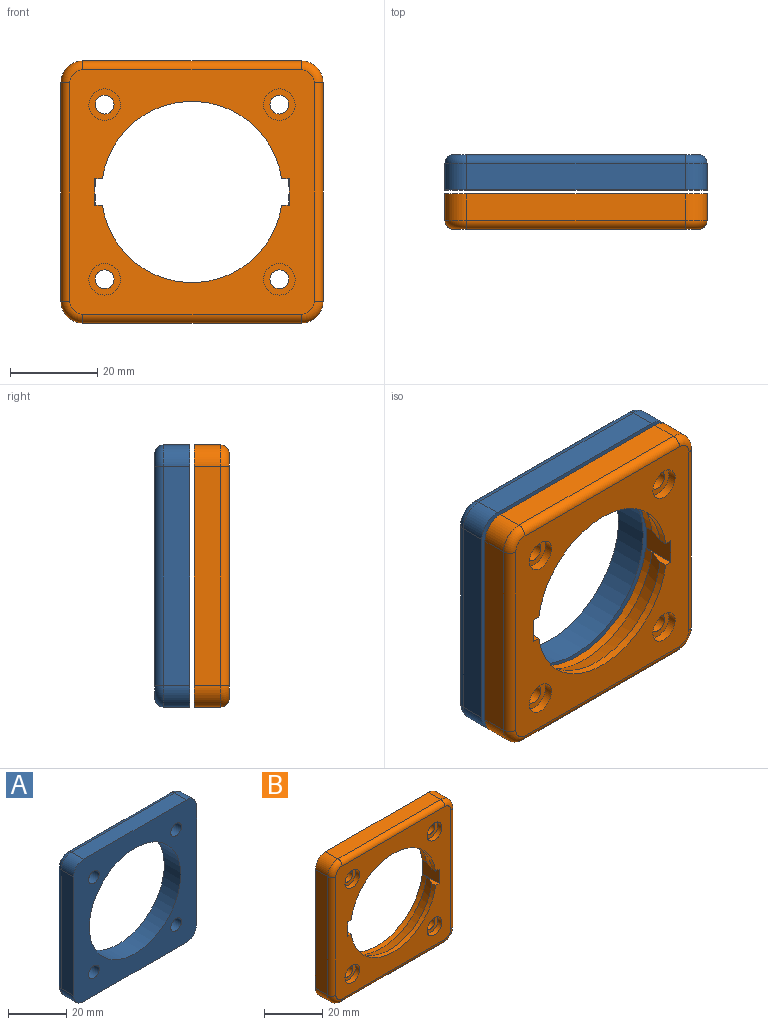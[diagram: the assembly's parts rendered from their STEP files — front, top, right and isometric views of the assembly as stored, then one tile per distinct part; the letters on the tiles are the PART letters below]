
ASSEMBLY  parts=2 mates=1
PART A: 23 faces, bbox 60.8x8x60.8 mm
  f0: plane 50x6mm, normal (-1,0,0), area 300mm2, adj f10,f11,f14,f22
  f1: plane 50x6mm, normal (0,0,1), area 300mm2, adj f10,f11,f12,f18
  f2: plane 50x6mm, normal (1,0,0), area 300mm2, adj f10,f12,f13,f15
  f3: cylinder r=22.25mm len=44.5mm, axis (0,-1,0), area 1118.4mm2, adj f9,f10
  f4: plane 50x6mm, normal (0,0,-1), area 300mm2, adj f10,f13,f14,f19
  f5: cylinder r=2.6mm len=8mm, axis (0,-1,0), area 130.7mm2, adj f9,f10
  f6: cylinder r=2.6mm len=8mm, axis (0,-1,0), area 130.7mm2, adj f9,f10
  f7: cylinder r=2.6mm len=8mm, axis (0,-1,0), area 130.7mm2, adj f9,f10
  f8: cylinder r=2.6mm len=8mm, axis (0,-1,0), area 130.7mm2, adj f9,f10
  f9: plane 56x56mm, normal (0,1,0), area 1488mm2, adj f3,f5,f6,f7,f8,f15,f16,f17
  f10: plane 60x60mm, normal (0,-1,0), area 1938.3mm2, adj f0,f1,f2,f3,f4,f5,f6,f7
  f11: cylinder r=5mm len=6mm, axis (0,1,0), area 47.1mm2, adj f0,f1,f10,f20
  f12: cylinder r=5mm len=6mm, axis (0,-1,0), area 47.1mm2, adj f1,f2,f10,f16
  f13: cylinder r=5mm len=6mm, axis (0,1,0), area 47.1mm2, adj f2,f4,f10,f17
  f14: cylinder r=5mm len=6mm, axis (0,-1,0), area 47.1mm2, adj f0,f4,f10,f21
  f15: cylinder r=2mm len=50mm, axis (0,0,1), area 157.1mm2, adj f2,f9,f16,f17
  f16: torus R=3mm, axis (0,1,0), area 21.1mm2, adj f9,f12,f15,f18
  f17: torus R=3mm, axis (0,1,0), area 21.1mm2, adj f9,f13,f15,f19
  f18: cylinder r=2mm len=50mm, axis (-1,0,0), area 157.1mm2, adj f1,f9,f16,f20
  f19: cylinder r=2mm len=50mm, axis (1,0,0), area 157.1mm2, adj f4,f9,f17,f21
  f20: torus R=3mm, axis (0,1,0), area 21.1mm2, adj f9,f11,f18,f22
  f21: torus R=3mm, axis (0,1,0), area 21.1mm2, adj f9,f14,f19,f22
  f22: cylinder r=2mm len=50mm, axis (0,0,-1), area 157.1mm2, adj f0,f9,f20,f21
PART B: 42 faces, bbox 60.8x8x60.8 mm
  f0: cylinder r=20.75mm len=41.06mm, axis (0,-1,0), area 106.5mm2, adj f2,f3,f36,f39
  f1: plane 60x60mm, normal (0,1,0), area 1964.4mm2, adj f5,f6,f8,f9,f10,f11,f12,f15
  f2: plane 56x56mm, normal (0,-1,0), area 1593.9mm2, adj f0,f7,f14,f17,f20,f23,f28,f29
  f3: cone r=22.25mm half-angle=20deg, axis (0,1,0), area 269.8mm2, adj f0,f5,f36,f39
  f4: cone r=22.25mm half-angle=20deg, axis (0,1,0), area 269.8mm2, adj f6,f7,f37,f41
  f5: cylinder r=22.25mm len=44.09mm, axis (0,-1,0), area 132.8mm2, adj f1,f3,f36,f39
  f6: cylinder r=22.25mm len=44.09mm, axis (0,-1,0), area 132.8mm2, adj f1,f4,f37,f41
  f7: cylinder r=20.75mm len=41.06mm, axis (0,-1,0), area 106.5mm2, adj f2,f4,f37,f41
  f8: plane 50x6mm, normal (0,0,1), area 300mm2, adj f1,f24,f27,f31
  f9: plane 50x6mm, normal (-1,0,0), area 300mm2, adj f1,f24,f25,f35
  f10: plane 50x6mm, normal (0,0,-1), area 300mm2, adj f1,f25,f26,f32
  f11: plane 50x6mm, normal (1,0,0), area 300mm2, adj f1,f26,f27,f28
  f12: cylinder r=2.15mm len=6mm, axis (0,-1,0), area 81.1mm2, adj f1,f13
  f13: plane 7.2x7.2mm, normal (0,-1,0), area 26.2mm2, adj f12,f14
  f14: cylinder r=3.6mm len=7.2mm, axis (0,-1,0), area 45.2mm2, adj f2,f13
  f15: cylinder r=2.15mm len=6mm, axis (0,-1,0), area 81.1mm2, adj f1,f16
  f16: plane 7.2x7.2mm, normal (0,-1,0), area 26.2mm2, adj f15,f17
  f17: cylinder r=3.6mm len=7.2mm, axis (0,-1,0), area 45.2mm2, adj f2,f16
  f18: cylinder r=2.15mm len=6mm, axis (0,-1,0), area 81.1mm2, adj f1,f19
  f19: plane 7.2x7.2mm, normal (0,-1,0), area 26.2mm2, adj f18,f20
  f20: cylinder r=3.6mm len=7.2mm, axis (0,-1,0), area 45.2mm2, adj f2,f19
  f21: cylinder r=2.15mm len=6mm, axis (0,-1,0), area 81.1mm2, adj f1,f22
  f22: plane 7.2x7.2mm, normal (0,-1,0), area 26.2mm2, adj f21,f23
  f23: cylinder r=3.6mm len=7.2mm, axis (0,-1,0), area 45.2mm2, adj f2,f22
  f24: cylinder r=5mm len=6mm, axis (0,1,0), area 47.1mm2, adj f1,f8,f9,f33
  f25: cylinder r=5mm len=6mm, axis (0,-1,0), area 47.1mm2, adj f1,f9,f10,f34
  f26: cylinder r=5mm len=6mm, axis (0,1,0), area 47.1mm2, adj f1,f10,f11,f30
  f27: cylinder r=5mm len=6mm, axis (0,-1,0), area 47.1mm2, adj f1,f8,f11,f29
  f28: cylinder r=2mm len=50mm, axis (0,0,1), area 157.1mm2, adj f2,f11,f29,f30
  f29: torus R=3mm, axis (0,-1,0), area 21.1mm2, adj f2,f27,f28,f31
  f30: torus R=3mm, axis (0,-1,0), area 21.1mm2, adj f2,f26,f28,f32
  f31: cylinder r=2mm len=50mm, axis (-1,0,0), area 157.1mm2, adj f2,f8,f29,f33
  f32: cylinder r=2mm len=50mm, axis (1,0,0), area 157.1mm2, adj f2,f10,f30,f34
  f33: torus R=3mm, axis (0,-1,0), area 21.1mm2, adj f2,f24,f31,f35
  f34: torus R=3mm, axis (0,-1,0), area 21.1mm2, adj f2,f25,f32,f35
  f35: cylinder r=2mm len=50mm, axis (0,0,-1), area 157.1mm2, adj f2,f9,f33,f34
  f36: plane 8.01x1.73mm, normal (0,0,-1), area 7.5mm2, adj f0,f1,f2,f3,f5,f38
  f37: plane 8.01x1.73mm, normal (0,0,1), area 7.5mm2, adj f1,f2,f4,f6,f7,f38
  f38: plane 8x6mm, normal (-1,0,0), area 48mm2, adj f1,f2,f36,f37
  f39: plane 8.01x1.73mm, normal (0,0,-1), area 7.5mm2, adj f0,f1,f2,f3,f5,f40
  f40: plane 8x6mm, normal (1,0,0), area 48mm2, adj f1,f2,f39,f41
  f41: plane 8.01x1.73mm, normal (0,0,1), area 7.5mm2, adj f1,f2,f4,f6,f7,f40
PLACE A t=(-17.55,-4.48,2.43)mm fixed
PLACE B t=(-17.55,-5.48,2.43)mm
MATE slider B.f18 <-> A.f6  axis (0,-1,0) through (2.45,2.52,-17.57)mm
